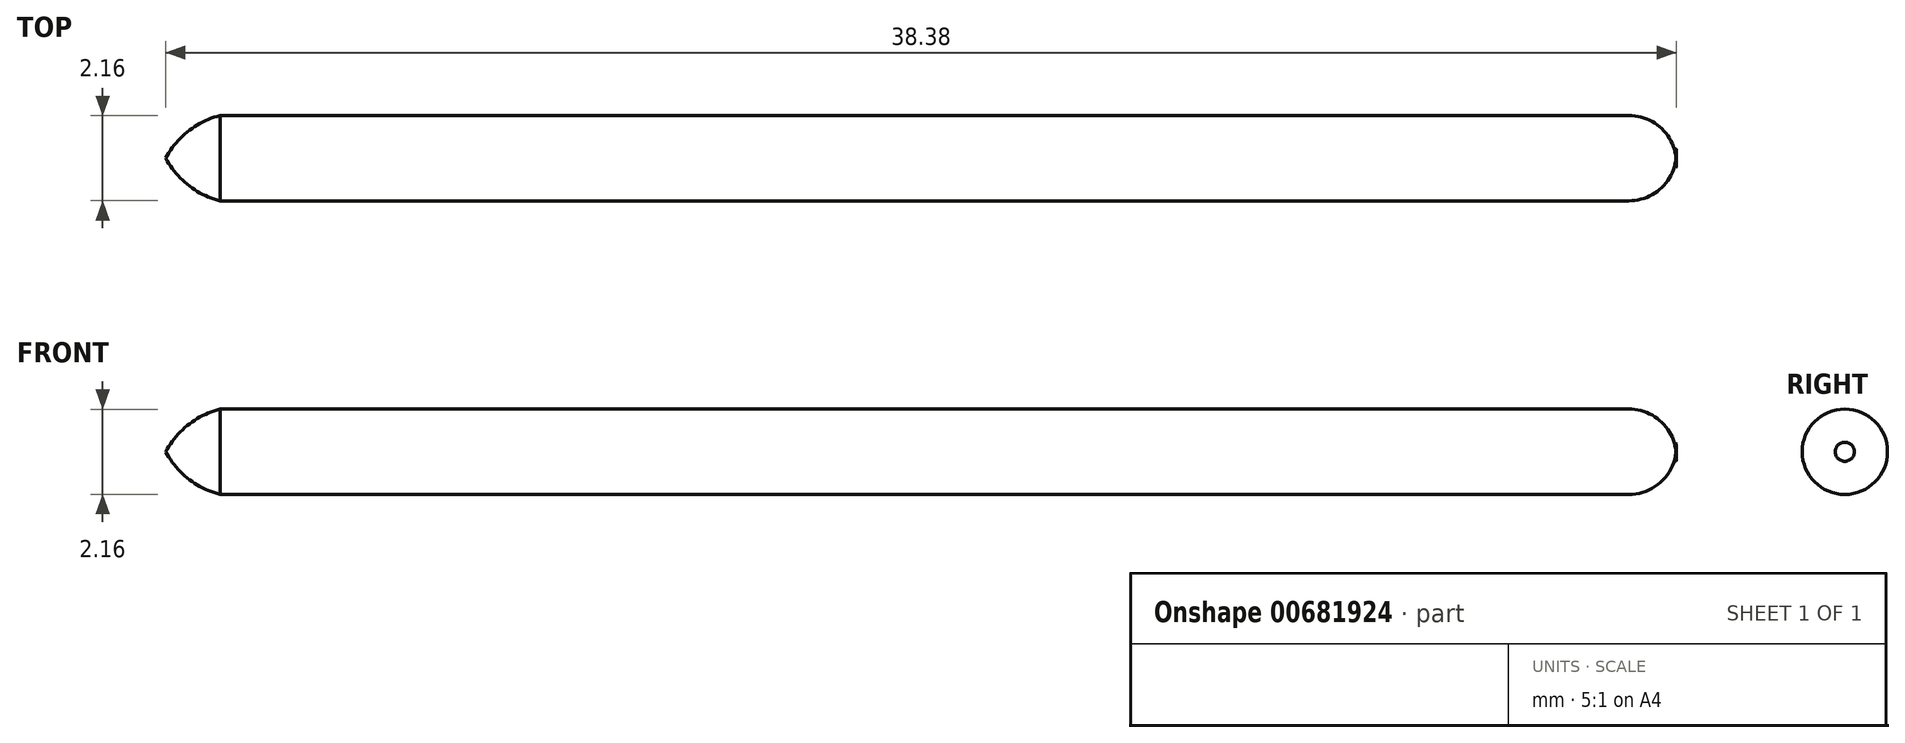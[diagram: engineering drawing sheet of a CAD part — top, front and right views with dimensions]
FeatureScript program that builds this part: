
annotation { "Feature Type Name" : "Feature", "Feature Type Description" : "" }
export const myFeature = defineFeature(function(context is Context, id is Id, definition is map)
    precondition{}
    {
        {
            var Q0;
            Q0=qCreatedBy(makeId("Front.planeOp"),FACE);
            var sketch = newSketch(context, id + "F0", { "sketchPlane" : qUnion([Q0])});
            skLineSegment(sketch, "E0", {"start": v(0, 0) * mm, "end": v(38.37, 0) * mm});
            skArc(sketch, "E1", {"start": v(1.38, 1.08) * mm, "mid": v(0.58, 0.69) * mm, "end": v(0, 0) * mm});
            skLineSegment(sketch, "E2", {"start": v(1.38, 1.08) * mm, "end": v(37.17, 1.08) * mm});
            skArc(sketch, "E3", {"start": v(38.37, 0) * mm, "mid": v(37.98, 0.77) * mm, "end": v(37.17, 1.08) * mm});
            skSolve(sketch);
        }
        {
            var Q0;
            Q0=makeQuery(id+"F0.imprint","IMPRINT",FACE,{"disambiguationData":[TD([[makeQuery(id+"F0.imprint","IMPRINT",EDGE,{"derivedFrom":sQuery(id+"F0.wireOp",EDGE,"E0")}),1.0]])]});
            var Q1;
            Q1=sQuery(id+"F0.wireOp",EDGE,"E0");
            revolve(context, id + "F1", {"entities" : qUnion([Q0]), "axis" : qUnion([Q1]), "revolveType" : RevolveType.FULL});
        }
    });
